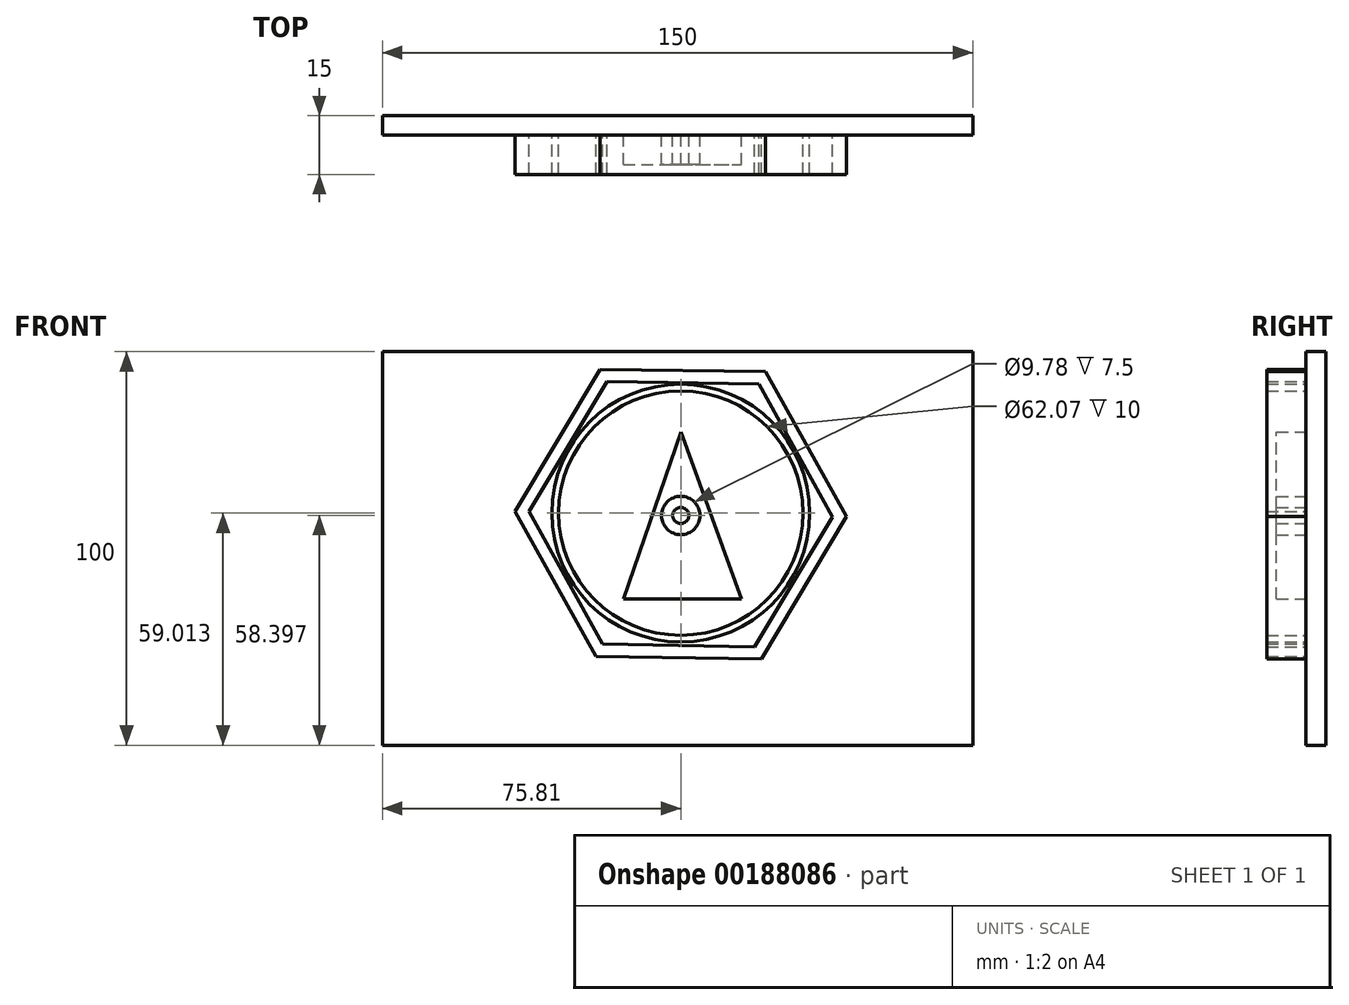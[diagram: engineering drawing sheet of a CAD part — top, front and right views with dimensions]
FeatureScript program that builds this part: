
annotation { "Feature Type Name" : "Feature", "Feature Type Description" : "" }
export const myFeature = defineFeature(function(context is Context, id is Id, definition is map)
    precondition{}
    {
        {
            var Q0;
            Q0=qCreatedBy(makeId("Front.planeOp"),FACE);
            var sketch = newSketch(context, id + "F0", { "sketchPlane" : qUnion([Q0])});
            skLineSegment(sketch, "E0.bottom", {"start": v(-75.81, -37.13) * mm, "end": v(74.19, -37.13) * mm});
            skLineSegment(sketch, "E0.top", {"start": v(-75.81, 62.87) * mm, "end": v(74.19, 62.87) * mm});
            skLineSegment(sketch, "E0.left", {"start": v(-75.81, -37.13) * mm, "end": v(-75.81, 62.87) * mm});
            skLineSegment(sketch, "E0.right", {"start": v(74.19, -37.13) * mm, "end": v(74.19, 62.87) * mm});
            skSolve(sketch);
        }
        {
            var Q0;
            Q0=makeQuery(id+"F0.imprint","IMPRINT",FACE,{"disambiguationData":[TD([[makeQuery(id+"F0.imprint","IMPRINT",EDGE,{"derivedFrom":sQuery(id+"F0.wireOp",EDGE,"E0.bottom")}),1.0]])]});
            extrude(context, id + "F1", {"entities" : qUnion([Q0]), "depth" : 5 * mm});
        }
        {
            var Q0;
            Q0=makeQuery(id+"F1.opExtrude","CAP_FACE",FACE,{"disambiguationData":[OSD([sQuery(id+"F0.wireOp",EDGE,"E0.bottom"),sQuery(id+"F0.wireOp",EDGE,"E0.top"),sQuery(id+"F0.wireOp",EDGE,"E0.left"),sQuery(id+"F0.wireOp",EDGE,"E0.right")])],"isStart":false});
            var sketch = newSketch(context, id + "F2", { "sketchPlane" : qUnion([Q0])});
            skLineSegment(sketch, "E1", {"start": v(-14.6, 0) * mm, "end": v(15.4, 0) * mm});
            skLineSegment(sketch, "E2", {"start": v(-14.6, 0) * mm, "end": v(0, 42.53) * mm});
            skLineSegment(sketch, "E3", {"start": v(0, 42.53) * mm, "end": v(15.4, 0) * mm});
            skCircle(sketch, "E4", {"center": v(0, 21.27) * mm, "radius": 4.9 * mm});
            skPoint(sketch, "E4.centerSnap0", {"position": v(-7.3, 21.27) * mm});
            skCircle(sketch, "E5", {"center": v(0, 21.27) * mm, "radius": 2.06 * mm});
            skSolve(sketch);
        }
        {
            var Q0;
            Q0 = qSketchRegion(id + "F2", true);
            var Q1;
            Q1=makeQuery(id+"F2.imprint","IMPRINT",FACE,{"disambiguationData":[TD([[makeQuery(id+"F2.imprint","IMPRINT",EDGE,{"derivedFrom":sQuery(id+"F2.wireOp",EDGE,"E5")}),1.0]])]});
            extrude(context, id + "F3", {"entities" : qUnion([Q0, Q1]), "operationType" : NewBodyOperationType.ADD, "depth" : 7.5 * mm});
        }
        {
            var Q0;
            {var subQ0=sQuery(id+"F0.wireOp",EDGE,"E0.right");var subQ1=sQuery(id+"F0.wireOp",EDGE,"E0.left");var subQ2=sQuery(id+"F0.wireOp",EDGE,"E0.top");var subQ3=sQuery(id+"F0.wireOp",EDGE,"E0.bottom");Q0=makeQuery(id+"F3.boolean.opBoolean","SPLIT",FACE,{"disambiguationData":[TD([makeQuery(id+"F1.opExtrude","SWEPT_FACE",FACE,{"disambiguationData":[OSD([subQ3])]})])],"derivedFrom":makeQuery(id+"F1.opExtrude","CAP_FACE",FACE,{"disambiguationData":[OSD([subQ3,subQ2,subQ1,subQ0])],"isStart":false})});}
            var sketch = newSketch(context, id + "F4", { "sketchPlane" : qUnion([Q0])});
            skCircle(sketch, "E6.cCircle", {"center": v(0, 21.64) * mm, "radius": 36.47 * mm, "construction": true});
            skLineSegment(sketch, "E6.0", {"start": v(-42.1, 22.24) * mm, "end": v(-20.53, 58.4) * mm});
            skLineSegment(sketch, "E6.1", {"start": v(-20.53, 58.4) * mm, "end": v(21.58, 57.8) * mm});
            skLineSegment(sketch, "E6.2", {"start": v(21.58, 57.8) * mm, "end": v(42.1, 21.03) * mm});
            skLineSegment(sketch, "E6.3", {"start": v(42.1, 21.03) * mm, "end": v(20.53, -15.13) * mm});
            skLineSegment(sketch, "E6.4", {"start": v(20.53, -15.13) * mm, "end": v(-21.58, -14.52) * mm});
            skLineSegment(sketch, "E6.5", {"start": v(-21.58, -14.52) * mm, "end": v(-42.1, 22.24) * mm});
            skPoint(sketch, "E6.0.midPoint", {"position": v(-31.32, 40.32) * mm});
            skCircle(sketch, "E7.cCircle", {"center": v(0, 21.64) * mm, "radius": 33.39 * mm, "construction": true});
            skLineSegment(sketch, "E7.0", {"start": v(-38.55, 22.33) * mm, "end": v(-18.68, 55.37) * mm});
            skLineSegment(sketch, "E7.1", {"start": v(-18.68, 55.37) * mm, "end": v(19.87, 54.67) * mm});
            skLineSegment(sketch, "E7.2", {"start": v(19.87, 54.67) * mm, "end": v(38.55, 20.95) * mm});
            skLineSegment(sketch, "E7.3", {"start": v(38.55, 20.95) * mm, "end": v(18.68, -12.1) * mm});
            skLineSegment(sketch, "E7.4", {"start": v(18.68, -12.1) * mm, "end": v(-19.87, -11.4) * mm});
            skLineSegment(sketch, "E7.5", {"start": v(-19.87, -11.4) * mm, "end": v(-38.55, 22.33) * mm});
            skPoint(sketch, "E7.0.midPoint", {"position": v(-28.61, 38.85) * mm});
            skSolve(sketch);
        }
        {
            var Q0;
            Q0 = qSketchRegion(id + "F4", true);
            extrude(context, id + "F5", {"entities" : qUnion([Q0]), "operationType" : NewBodyOperationType.ADD, "depth" : 10 * mm});
        }
        {
            var Q0;
            {var subQ0=sQuery(id+"F0.wireOp",EDGE,"E0.right");var subQ2=sQuery(id+"F0.wireOp",EDGE,"E0.left");var subQ4=sQuery(id+"F0.wireOp",EDGE,"E0.top");var subQ6=sQuery(id+"F0.wireOp",EDGE,"E0.bottom");var subQ7=makeQuery(id+"F1.opExtrude","SWEPT_FACE",FACE,{"disambiguationData":[OSD([subQ6])]});Q0=makeQuery(id+"F5.boolean.opBoolean","SPLIT",FACE,{"disambiguationData":[TD([subQ7])],"derivedFrom":makeQuery(id+"F3.boolean.opBoolean","SPLIT",FACE,{"disambiguationData":[TD([subQ7])],"derivedFrom":makeQuery(id+"F1.opExtrude","CAP_FACE",FACE,{"disambiguationData":[OSD([subQ6,subQ4,subQ2,subQ0])],"isStart":false})})});}
            var sketch = newSketch(context, id + "F6", { "sketchPlane" : qUnion([Q0])});
            skCircle(sketch, "E8", {"center": v(0, 21.88) * mm, "radius": 32.75 * mm});
            skCircle(sketch, "E9", {"center": v(0, 21.88) * mm, "radius": 31.03 * mm});
            skSolve(sketch);
        }
        {
            var Q0;
            Q0 = qSketchRegion(id + "F6", true);
            extrude(context, id + "F7", {"entities" : qUnion([Q0]), "operationType" : NewBodyOperationType.ADD, "depth" : 10 * mm});
        }
    });
